# Revit family: Washer_Continental-Girbau_MG-Series
name_source: partatom
category: Mechanical Equipment
units: mm (PartAtom-declared; Revit-internal decimal feet)

## family parameters
Always vertical = No
Classification Number = 23.45.70.11.14.14
Cut with Voids When Loaded = No
Maintain Annotation Orientation = No
Part Type = Normal
Room Calculation Point = No
Round Connector Dimension = Use Radius
Shared = No
Work Plane-Based = Yes

## types (1)
- Washer_Continental-Girbau_MG-Series
    Accent Material = Metal - Continental Girbau - Black
    Assembly Code = E1010610
    Capacity = as Specified
    Cold Water Connection Diameter = 0' - 0 3/4"
    Construction Details = http://arcat.com
    Cylinder Depth = 1' - 9 5/8"
    Cylinder Diameter = 2' - 0 13/32"
    Cylinder Volume = as Specified
    Default Elevation = 0' - 0"
    Description = Continental Girbau Commercial Washer as Specified
    Door Base Elevation = 1' - 7 11/16"
    Door Opening = 1' - 0 7/8"
    Door Opening Depth = 2' - 0"
    Drain Connection Diameter = 0' - 3"
    Electrical_Amperage = 0 A
    Electrical_Frequency = 0 Hz
    Electrical_Phase = 0
    Electrical_Voltage = 0 V
    Expected Lifespan (Years) = 0
    Fixture Finish = Metal - Continental Girbau - Silver
    Green Building-LEED = http://arcat.com
    Hot Water Connection Diameter = 0' - 0 3/4"
    Keynote = 11110
    Machine Function = as Specified
    Maintenance Schedule (Months) = 0
    Manufacturer = Continental Girbau, Inc.
    Manufacturer Fax = 920-231-4666
    Manufacturer Website = http://www.continentalgirbau.com
    Model = As Specified
    Product Data = http://arcat.com
    Revision = R1_05-2014
    Sales Information = http://www.continentalgirbau.com
    Send Message = http://www.arcat.com &amp;mf=
    Sound Pressure = as Specified
    SpecWizard = http://arcat.com
    Specification = http://arcat.com
    Standards Conformance = as Specified
    Steam Inlet Connection Diameter = 0' - 1"
    URL = http://www.continentalgirbau.com
    Unit Depth = 3' - 4"
    Unit Height = 4' - 4 3/16"
    Unit Weight = 0
    Unit Weight_Dynamic Load = 0
    Unit Weight_Live Load = 0
    Unit Width = 2' - 5 1/2"
    Warranty Duration (Years) = 0
    dcwrad = 0' - 0 3/8"
    dhwrad = 0' - 0 3/8"
    dooropeningactual = 1' - 3 7/8"
    drainrad = 0' - 1 1/2"
    halfdoor = 0' - 8 3/16"

## geometry (parser evidence)
native form markers: Blend x3, Sweep x2
no freeform markers — native parametric forms only
